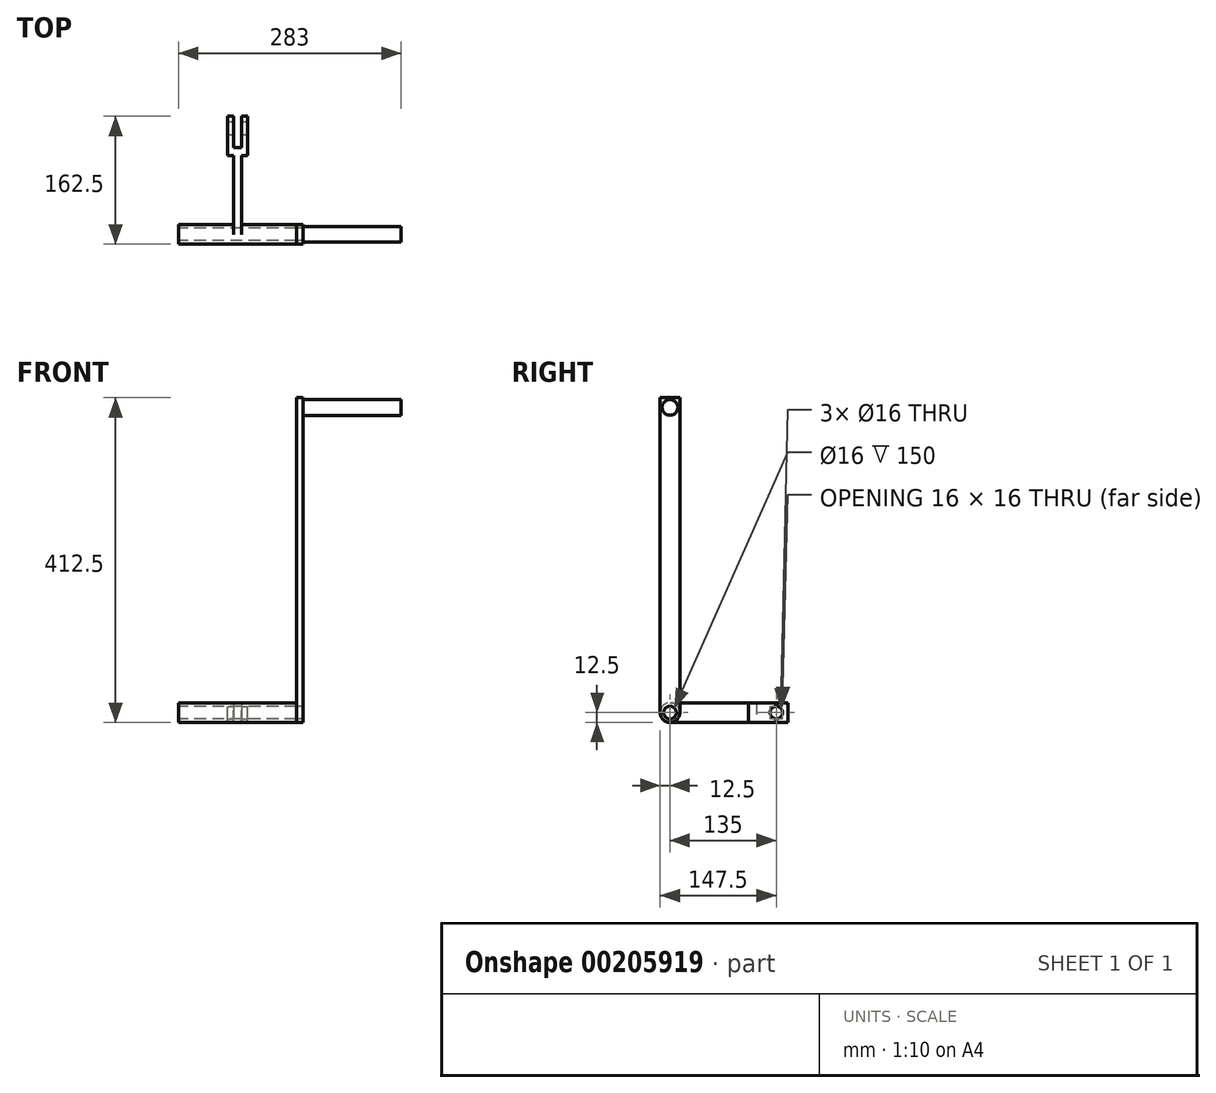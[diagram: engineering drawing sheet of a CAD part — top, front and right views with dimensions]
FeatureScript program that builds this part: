
annotation { "Feature Type Name" : "Feature", "Feature Type Description" : "" }
export const myFeature = defineFeature(function(context is Context, id is Id, definition is map)
    precondition{}
    {
        {
            var Q0;
            Q0=qCreatedBy(makeId("Right.planeOp"),FACE);
            var sketch = newSketch(context, id + "F0", { "sketchPlane" : qUnion([Q0])});
            skCircle(sketch, "E0", {"center": v(0, 0) * mm, "radius": 12.5 * mm});
            skCircle(sketch, "E1", {"center": v(0, 0) * mm, "radius": 8 * mm});
            skSolve(sketch);
        }
        {
            var Q0;
            Q0=makeQuery(id+"F0.imprint","IMPRINT",FACE,{"disambiguationData":[TD([[makeQuery(id+"F0.imprint","IMPRINT",EDGE,{"derivedFrom":sQuery(id+"F0.wireOp",EDGE,"E0")}),1.0]])]});
            extrude(context, id + "F1", {"entities" : qUnion([Q0]), "depth" : 75 * mm, "hasSecondDirection" : true, "secondDirectionOppositeDirection" : true, "secondDirectionDepth" : 75 * mm});
        }
        {
            var Q0;
            Q0=makeQuery(id+"F1.opExtrude","CAP_FACE",FACE,{"disambiguationData":[OSD([sQuery(id+"F0.wireOp",EDGE,"E0"),sQuery(id+"F0.wireOp",EDGE,"E1")])],"isStart":false});
            var sketch = newSketch(context, id + "F2", { "sketchPlane" : qUnion([Q0])});
            skLineSegment(sketch, "E2.bottom", {"start": v(12.5, 0) * mm, "end": v(-12.5, 0) * mm});
            skLineSegment(sketch, "E2.top", {"start": v(12.5, 400) * mm, "end": v(-12.5, 400) * mm});
            skLineSegment(sketch, "E2.left", {"start": v(12.5, 0) * mm, "end": v(12.5, 400) * mm});
            skLineSegment(sketch, "E2.right", {"start": v(-12.5, 0) * mm, "end": v(-12.5, 400) * mm});
            skPoint(sketch, "E2.middle", {"position": v(0, 200) * mm});
            skSolve(sketch);
        }
        {
            var Q0;
            Q0=makeQuery(id+"F2.imprint","IMPRINT",FACE,{"disambiguationData":[TD([[makeQuery(id+"F2.imprint","IMPRINT",EDGE,{"derivedFrom":sQuery(id+"F2.wireOp",EDGE,"E2.top")}),1.0]])]});
            var Q1;
            {var subQ0=sQuery(id+"F2.wireOp",EDGE,"E2.bottom");var subQ3=makeQuery(id+"F1.opExtrude","CAP_EDGE",EDGE,{"disambiguationData":[OSD([sQuery(id+"F0.wireOp",EDGE,"E1")])],"isStart":false});var subQ4=makeQuery(id+"F2.imprint","INTERSECT",VERTEX,{"disambiguationData":[OD(0.0)],"derivedFrom":[subQ3,subQ0]});Q1=makeQuery(id+"F2.imprint","IMPRINT",FACE,{"disambiguationData":[TD([[makeQuery(id+"F2.imprint","IMPRINT",EDGE,{"disambiguationData":[TD([[subQ4,-1.0]])],"derivedFrom":subQ3}),-1.0]])]});}
            var Q2;
            {var subQ0=sQuery(id+"F2.wireOp",EDGE,"E2.bottom");var subQ3=makeQuery(id+"F1.opExtrude","CAP_EDGE",EDGE,{"disambiguationData":[OSD([sQuery(id+"F0.wireOp",EDGE,"E1")])],"isStart":false});var subQ4=makeQuery(id+"F2.imprint","INTERSECT",VERTEX,{"disambiguationData":[OD(0.0)],"derivedFrom":[subQ3,subQ0]});Q2=makeQuery(id+"F2.imprint","IMPRINT",FACE,{"disambiguationData":[TD([[makeQuery(id+"F2.imprint","IMPRINT",EDGE,{"disambiguationData":[TD([[subQ4,1.0]])],"derivedFrom":subQ3}),-1.0]])]});}
            extrude(context, id + "F3", {"entities" : qUnion([Q0, Q1, Q2]), "depth" : 8 * mm});
        }
        {
            var Q0;
            Q0=qCreatedBy(makeId("Right.planeOp"),FACE);
            var sketch = newSketch(context, id + "F4", { "sketchPlane" : qUnion([Q0])});
            skLineSegment(sketch, "E3.bottom", {"start": v(0, 12.5) * mm, "end": v(100, 12.5) * mm});
            skLineSegment(sketch, "E3.top", {"start": v(0, -12.5) * mm, "end": v(100, -12.5) * mm});
            skLineSegment(sketch, "E3.left", {"start": v(0, 12.5) * mm, "end": v(0, -12.5) * mm});
            skLineSegment(sketch, "E3.right", {"start": v(100, 12.5) * mm, "end": v(100, -12.5) * mm});
            skPoint(sketch, "E3.middle", {"position": v(50, 0) * mm});
            skSolve(sketch);
        }
        {
            var Q0;
            Q0=makeQuery(id+"F4.imprint","IMPRINT",FACE,{"disambiguationData":[TD([[makeQuery(id+"F4.imprint","IMPRINT",EDGE,{"derivedFrom":sQuery(id+"F4.wireOp",EDGE,"E3.bottom")}),-1.0]])]});
            extrude(context, id + "F5", {"entities" : qUnion([Q0]), "operationType" : NewBodyOperationType.ADD, "oppositeDirection" : true, "depth" : 5 * mm, "hasSecondDirection" : true, "secondDirectionOppositeDirection" : false, "secondDirectionDepth" : 5 * mm});
        }
        {
            var Q0;
            Q0=makeQuery(id+"F5.opExtrude","SWEPT_FACE",FACE,{"disambiguationData":[OSD([sQuery(id+"F4.wireOp",EDGE,"E3.right")])]});
            var sketch = newSketch(context, id + "F6", { "sketchPlane" : qUnion([Q0])});
            skLineSegment(sketch, "E4.bottom", {"start": v(12.5, -12.5) * mm, "end": v(-12.5, -12.5) * mm});
            skLineSegment(sketch, "E4.top", {"start": v(12.5, 12.5) * mm, "end": v(-12.5, 12.5) * mm});
            skLineSegment(sketch, "E4.left", {"start": v(12.5, -12.5) * mm, "end": v(12.5, 12.5) * mm});
            skLineSegment(sketch, "E4.right", {"start": v(-12.5, -12.5) * mm, "end": v(-12.5, 12.5) * mm});
            skPoint(sketch, "E4.middle", {"position": v(0, 0) * mm});
            skSolve(sketch);
        }
        {
            var Q0;
            {var subQ2=sQuery(id+"F6.wireOp",EDGE,"E4.right");Q0=makeQuery(id+"F6.imprint","IMPRINT",FACE,{"disambiguationData":[TD([[makeQuery(id+"F6.imprint","IMPRINT",EDGE,{"derivedFrom":subQ2}),-1.0]])]});}
            var Q1;
            {var subQ1=sQuery(id+"F4.wireOp",EDGE,"E3.right");var subQ2=makeQuery(id+"F5.opExtrude","CAP_EDGE",EDGE,{"disambiguationData":[OSD([subQ1])],"isStart":true});Q1=makeQuery(id+"F6.imprint","IMPRINT",FACE,{"disambiguationData":[TD([[makeQuery(id+"F6.imprint","IMPRINT",EDGE,{"derivedFrom":subQ2}),1.0]])]});}
            var Q2;
            {var subQ2=sQuery(id+"F6.wireOp",EDGE,"E4.left");Q2=makeQuery(id+"F6.imprint","IMPRINT",FACE,{"disambiguationData":[TD([[makeQuery(id+"F6.imprint","IMPRINT",EDGE,{"derivedFrom":subQ2}),1.0]])]});}
            extrude(context, id + "F7", {"entities" : qUnion([Q0, Q1, Q2]), "operationType" : NewBodyOperationType.ADD, "depth" : 10 * mm});
        }
        {
            var Q0;
            Q0=makeQuery(id+"F7.opExtrude","CAP_FACE",FACE,{"disambiguationData":[OSD([sQuery(id+"F6.wireOp",EDGE,"E4.bottom"),sQuery(id+"F6.wireOp",EDGE,"E4.top"),sQuery(id+"F6.wireOp",EDGE,"E4.left"),sQuery(id+"F6.wireOp",EDGE,"E4.right")])],"isStart":false});
            var sketch = newSketch(context, id + "F8", { "sketchPlane" : qUnion([Q0])});
            skLineSegment(sketch, "E5.bottom", {"start": v(-12.5, 12.5) * mm, "end": v(-5, 12.5) * mm});
            skLineSegment(sketch, "E5.top", {"start": v(-12.5, -12.5) * mm, "end": v(-5, -12.5) * mm});
            skLineSegment(sketch, "E5.left", {"start": v(-12.5, 12.5) * mm, "end": v(-12.5, -12.5) * mm});
            skLineSegment(sketch, "E5.right", {"start": v(-5, 12.5) * mm, "end": v(-5, -12.5) * mm});
            skLineSegment(sketch, "E6.bottom", {"start": v(12.5, 12.5) * mm, "end": v(5, 12.5) * mm});
            skLineSegment(sketch, "E6.top", {"start": v(12.5, -12.5) * mm, "end": v(5, -12.5) * mm});
            skLineSegment(sketch, "E6.left", {"start": v(12.5, 12.5) * mm, "end": v(12.5, -12.5) * mm});
            skLineSegment(sketch, "E6.right", {"start": v(5, 12.5) * mm, "end": v(5, -12.5) * mm});
            skSolve(sketch);
        }
        {
            var Q0;
            Q0=makeQuery(id+"F8.imprint","IMPRINT",FACE,{"disambiguationData":[TD([[makeQuery(id+"F8.imprint","IMPRINT",EDGE,{"derivedFrom":sQuery(id+"F8.wireOp",EDGE,"E5.bottom")}),1.0]])]});
            var Q1;
            Q1=makeQuery(id+"F8.imprint","IMPRINT",FACE,{"disambiguationData":[TD([[makeQuery(id+"F8.imprint","IMPRINT",EDGE,{"derivedFrom":sQuery(id+"F8.wireOp",EDGE,"E6.bottom")}),1.0]])]});
            extrude(context, id + "F9", {"entities" : qUnion([Q0, Q1]), "operationType" : NewBodyOperationType.ADD, "depth" : 40 * mm});
        }
        {
            var Q0;
            Q0=makeQuery(id+"F9.boolean.opBoolean","MERGE",FACE,{"derivedFrom":[makeQuery(id+"F7.opExtrude","SWEPT_FACE",FACE,{"disambiguationData":[OSD([sQuery(id+"F6.wireOp",EDGE,"E4.right")])]}),makeQuery(id+"F9.opExtrude","SWEPT_FACE",FACE,{"disambiguationData":[OSD([sQuery(id+"F8.wireOp",EDGE,"E5.left")])]})]});
            var sketch = newSketch(context, id + "F10", { "sketchPlane" : qUnion([Q0])});
            skCircle(sketch, "E7", {"center": v(135, 0) * mm, "radius": 8 * mm});
            skSolve(sketch);
        }
        {
            var Q0;
            Q0=makeQuery(id+"F10.imprint","IMPRINT",FACE,{"disambiguationData":[TD([[makeQuery(id+"F10.imprint","IMPRINT",EDGE,{"derivedFrom":sQuery(id+"F10.wireOp",EDGE,"E7")}),1.0]])]});
            extrude(context, id + "F11", {"entities" : qUnion([Q0]), "operationType" : NewBodyOperationType.REMOVE, "oppositeDirection" : true, "depth" : 66.2 * mm});
        }
        {
            var Q0;
            {var subQ0=sQuery(id+"F4.wireOp",EDGE,"E3.left");Q0=makeQuery(id+"F5.boolean.opBoolean","SPLIT",FACE,{"disambiguationData":[TD([makeQuery(id+"F1.opExtrude","SWEPT_FACE",FACE,{"disambiguationData":[OSD([sQuery(id+"F0.wireOp",EDGE,"E1")])]})])],"derivedFrom":makeQuery(id+"F5.opExtrude","CAP_FACE",FACE,{"disambiguationData":[OSD([sQuery(id+"F4.wireOp",EDGE,"E3.bottom"),sQuery(id+"F4.wireOp",EDGE,"E3.top"),subQ0,sQuery(id+"F4.wireOp",EDGE,"E3.right")])],"isStart":true})});}
            extrude(context, id + "F12", {"entities" : qUnion([Q0]), "operationType" : NewBodyOperationType.REMOVE, "oppositeDirection" : true, "depth" : 25 * mm});
        }
        {
            var Q0;
            Q0=makeQuery(id+"F3.opExtrude","CAP_FACE",FACE,{"disambiguationData":[OSD([sQuery(id+"F0.wireOp",EDGE,"E0"),sQuery(id+"F0.wireOp",EDGE,"E1"),sQuery(id+"F2.wireOp",EDGE,"E2.top"),sQuery(id+"F2.wireOp",EDGE,"E2.left"),sQuery(id+"F2.wireOp",EDGE,"E2.right")])],"isStart":false});
            var sketch = newSketch(context, id + "F13", { "sketchPlane" : qUnion([Q0])});
            skCircle(sketch, "E8", {"center": v(0, 387.67) * mm, "radius": 10 * mm});
            skSolve(sketch);
        }
        {
            var Q0;
            Q0=makeQuery(id+"F13.imprint","IMPRINT",FACE,{"disambiguationData":[TD([[makeQuery(id+"F13.imprint","IMPRINT",EDGE,{"derivedFrom":sQuery(id+"F13.wireOp",EDGE,"E8")}),1.0]])]});
            extrude(context, id + "F14", {"entities" : qUnion([Q0]), "operationType" : NewBodyOperationType.ADD, "depth" : 125 * mm});
        }
    });
